# Revit family: ev450rtv_2_13_23
name_source: partatom
category: Mechanical Equipment
units: mm (PartAtom-declared; Revit-internal decimal feet)

## family parameters
Always vertical = Yes
Cut with Voids When Loaded = No
OmniClass Number = 23.75.00.00
OmniClass Title = Climate Control (HVAC)
Part Type = Normal
Room Calculation Point = No
Round Connector Dimension = Use Diameter
Shared = No
Work Plane-Based = No

## types (7) — shared parameters
Manufacturer = RenewAire
Model = EV450RTV
URL = http://www.renewaire.com

## per-type parameters (varying)
| type | Number of Poles | Phase | Phase Scheduled | Voltage | Voltage Scheduled | Voltage Workaround |
| 208 V Single Phase | 2 | 1 | 1 | 208 V | 208 V | 208 |
| 230 V Single Phase | 2 | 1 | 1 | 230 V | 230 V | 230 |
| 115 V Single Phase | 1 | 1 | 1 | 115 V | 115 V | 115 |
| 277 V Single Phase | 1 | 1 | 1 | 277 V | 277 V | 277 |
| 208 V Three Phase | 3 | 3 | 3 | 208 V | 208 V | 208 |
| 230 V Three Phase | 3 | 3 | 3 | 230 V | 230 V | 230 |
| 460 V Three Phase | 3 | 3 | 3 | 460 V | 460 V | 460 |

## geometry (parser evidence)
native form markers: Sweep x3
no freeform markers — native parametric forms only
